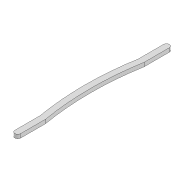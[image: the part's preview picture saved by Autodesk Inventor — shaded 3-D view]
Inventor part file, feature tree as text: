
AUTODESK INVENTOR PART (.ipt)
format: ipt  version: 2022 (Build 260153000, 153)  size: 99,840 bytes
history: native  units: mm
features: extrude x1, sketch x1
ambient origin geometry x8: Origin, YZ Plane, XZ Plane, XY Plane, X Axis, Y Axis, Z Axis, Center Point
bodies: Solid1 (feature_tree)
feature tree (2):
  extrude  "Extrusion1"  Depth=300.0mm
  sketch  "Sketch1"  dims[d0=2.2mm d1=2.2mm d2=6.0mm d3=153.89mm d6=4.0mm d7=0.0mm d10=2.2mm d11=25.907mm d12=2.2mm d13=127.773mm d16=300.0mm d17=300.0mm]
